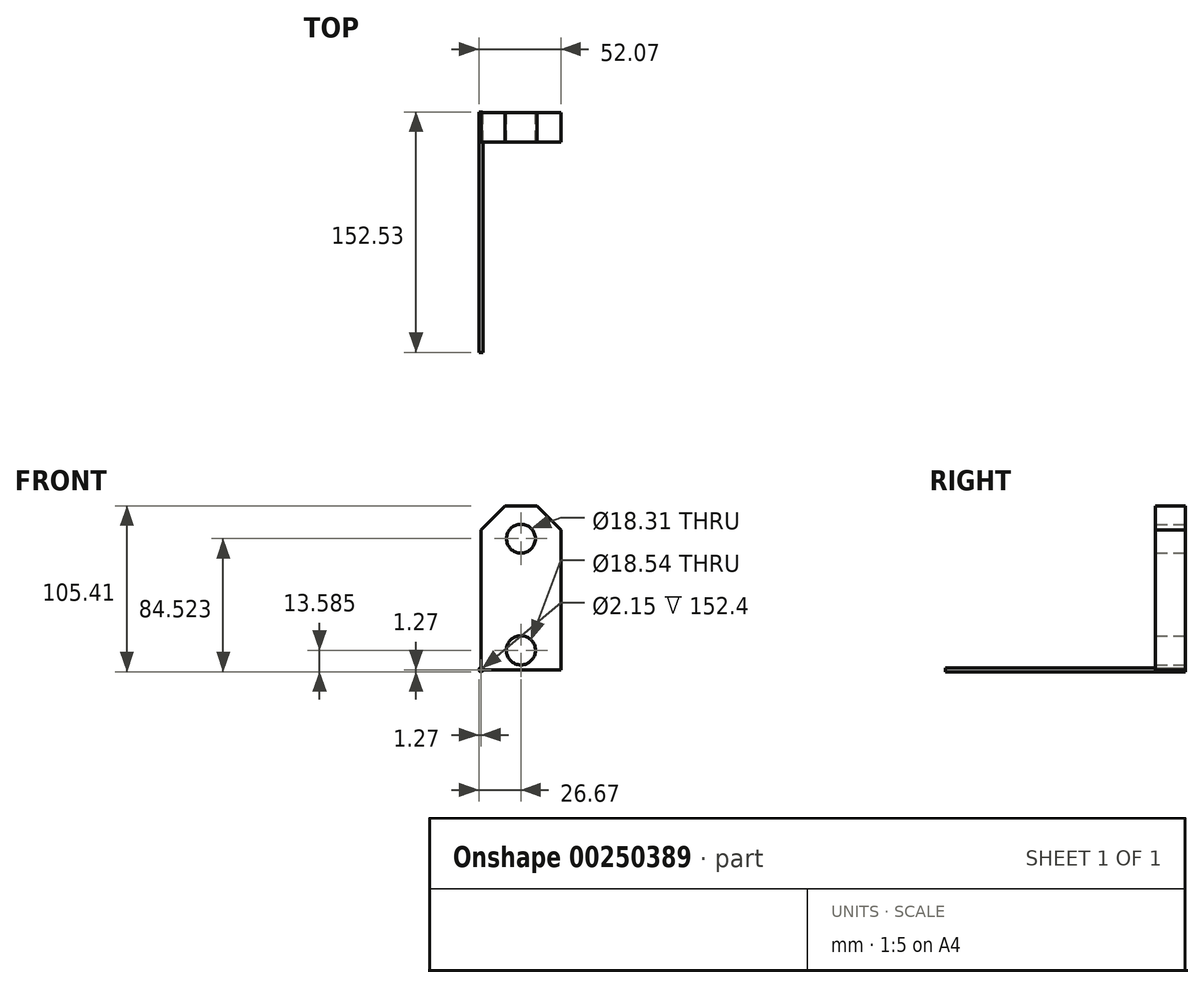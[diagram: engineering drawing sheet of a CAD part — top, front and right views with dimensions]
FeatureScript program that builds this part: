
annotation { "Feature Type Name" : "Feature", "Feature Type Description" : "" }
export const myFeature = defineFeature(function(context is Context, id is Id, definition is map)
    precondition{}
    {
        {
            var Q0;
            Q0=qCreatedBy(makeId("Front.planeOp"),FACE);
            var sketch = newSketch(context, id + "F0", { "sketchPlane" : qUnion([Q0])});
            skCircle(sketch, "E0", {"center": v(0, 0) * mm, "radius": 1.27 * mm});
            skCircle(sketch, "E1", {"center": v(0, 0) * mm, "radius": 1.08 * mm});
            skSolve(sketch);
        }
        {
            var Q0;
            Q0 = qSketchRegion(id + "F0", true);
            extrude(context, id + "F1", {"entities" : qUnion([Q0]), "depth" : 152.4 * mm});
        }
        {
            var Q0;
            Q0=makeQuery(id+"F0.imprint","IMPRINT",FACE,{"disambiguationData":[TD([[makeQuery(id+"F0.imprint","IMPRINT",EDGE,{"derivedFrom":sQuery(id+"F0.wireOp",EDGE,"E1")}),1.0]])]});
            extrude(context, id + "F2", {"entities" : qUnion([Q0]), "oppositeDirection" : true, "depth" : 0.13 * mm});
        }
        {
            var Q0;
            Q0=qCreatedBy(makeId("Front.planeOp"),FACE);
            var sketch = newSketch(context, id + "F3", { "sketchPlane" : qUnion([Q0])});
            skLineSegment(sketch, "E2", {"start": v(0, 0) * mm, "end": v(50.8, 0) * mm});
            skLineSegment(sketch, "E3", {"start": v(50.8, 0) * mm, "end": v(50.8, 104.14) * mm});
            skLineSegment(sketch, "E4", {"start": v(0, 0) * mm, "end": v(0, 104.14) * mm});
            skLineSegment(sketch, "E5", {"start": v(0, 104.14) * mm, "end": v(50.8, 104.14) * mm});
            skCircle(sketch, "E6", {"center": v(25.4, 83.25) * mm, "radius": 9.16 * mm});
            skCircle(sketch, "E7", {"center": v(25.4, 12.32) * mm, "radius": 9.27 * mm});
            skPoint(sketch, "E8.orphan", {"position": v(25.4, 104.14) * mm});
            skPoint(sketch, "E9.orphan", {"position": v(50.8, 83.25) * mm});
            skPoint(sketch, "E10.orphan", {"position": v(0, 83.25) * mm});
            skPoint(sketch, "E11.orphan", {"position": v(0, 12.32) * mm});
            skPoint(sketch, "E12.orphan", {"position": v(50.8, 12.32) * mm});
            skPoint(sketch, "E13.orphan", {"position": v(25.4, 0) * mm});
            skSolve(sketch);
        }
        {
            var Q0;
            Q0 = qSketchRegion(id + "F3", true);
            extrude(context, id + "F4", {"entities" : qUnion([Q0]), "depth" : 19 * mm});
        }
        {
            var Q0;
            Q0=makeQuery(id+"F4.opExtrude","SWEPT_EDGE",EDGE,{"disambiguationData":[OSD([sQuery(id+"F3.wireOp",EDGE,"E3"),sQuery(id+"F3.wireOp",EDGE,"E5")])]});
            chamfer(context, id + "F5", {"entities" : qUnion([Q0]), "width" : 15.24 * mm, "tangentPropagation" : true});
        }
        {
            var Q0;
            Q0=makeQuery(id+"F4.opExtrude","SWEPT_EDGE",EDGE,{"disambiguationData":[OSD([sQuery(id+"F3.wireOp",EDGE,"E4"),sQuery(id+"F3.wireOp",EDGE,"E5")])]});
            chamfer(context, id + "F6", {"entities" : qUnion([Q0]), "width" : 15.24 * mm, "tangentPropagation" : true});
        }
    });
